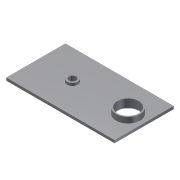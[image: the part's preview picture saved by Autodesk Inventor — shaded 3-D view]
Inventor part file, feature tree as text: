
AUTODESK INVENTOR PART (.ipt)
format: ipt  version: 2012 (Build 160160000, 160)  size: 99,328 bytes
history: native  units: mm
features: extrude x3, sketch x3
ambient origin geometry x8: Origin, YZ Plane, XZ Plane, XY Plane, X Axis, Y Axis, Z Axis, Center Point
bodies: Solid1 (feature_tree)
feature tree (6):
  extrude  "Extrusion1"  Depth=66.2mm
  extrude  "Extrusion2"  Depth=8.0mm
  extrude  "Extrusion3"  Depth=18.0mm
  sketch  "Sketch1"  dims[d0=121.2mm d1=66.2mm]
  sketch  "Sketch2"  dims[d3=33.1mm d4=8.0mm]
  sketch  "Sketch3"  dims[d5=23.8mm d6=18.0mm d7=41.0mm d8=3.0mm d9=0.0mm d10=12.0mm d11=3.0mm d12=0.0mm d13=23.8mm d14=26.8mm d15=6.4mm d16=0.0mm]
